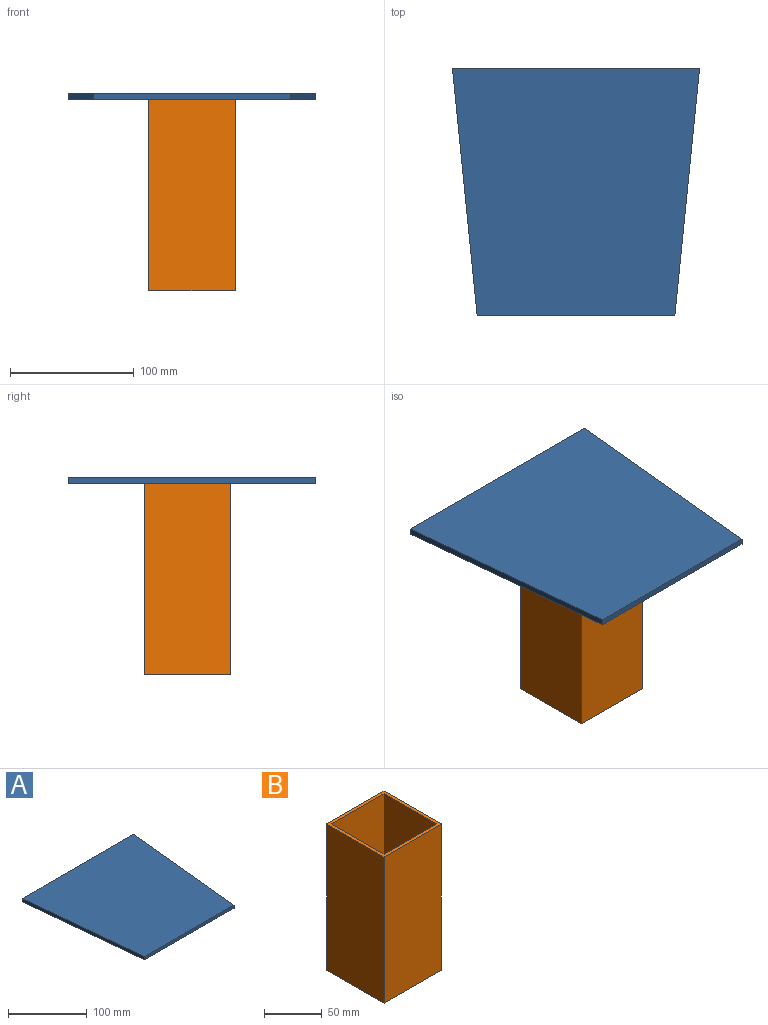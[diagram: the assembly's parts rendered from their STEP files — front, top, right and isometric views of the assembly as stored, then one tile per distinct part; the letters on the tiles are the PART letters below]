
ASSEMBLY  parts=2 mates=1
PART A: 6 faces, bbox 200x200x5 mm
  f0: plane 160x5mm, normal (0,-1,0), area 800mm2, adj f1,f3,f4,f5
  f1: plane 200x20mm, normal (1,-0.1,0), area 1005mm2, adj f0,f2,f4,f5
  f2: plane 200x5mm, normal (0,1,0), area 1000mm2, adj f1,f3,f4,f5
  f3: plane 200x20mm, normal (-1,-0.1,0), area 1005mm2, adj f0,f2,f4,f5
  f4: plane 200x200mm, normal (0,0,1), area 36000mm2, adj f0,f1,f2,f3
  f5: plane 200x200mm, normal (0,0,-1), area 36000mm2, adj f0,f1,f2,f3
PART B: 10 faces, bbox 70x70x155 mm
  f0: plane 155x64mm, normal (1,0,0), area 9920mm2, adj f1,f7,f8,f9
  f1: plane 155x64mm, normal (0,-1,0), area 9920mm2, adj f0,f2,f8,f9
  f2: plane 155x64mm, normal (-1,0,0), area 9920mm2, adj f1,f7,f8,f9
  f3: plane 155x70mm, normal (1,0,0), area 10850mm2, adj f4,f6,f8,f9
  f4: plane 155x70mm, normal (0,1,0), area 10850mm2, adj f3,f5,f8,f9
  f5: plane 155x70mm, normal (-1,0,0), area 10850mm2, adj f4,f6,f8,f9
  f6: plane 155x70mm, normal (0,-1,0), area 10850mm2, adj f3,f5,f8,f9
  f7: plane 155x64mm, normal (0,1,0), area 9920mm2, adj f0,f2,f8,f9
  f8: plane 70x70mm, normal (0,0,-1), area 804mm2, adj f0,f1,f2,f3,f4,f5,f6,f7
  f9: plane 70x70mm, normal (0,0,1), area 804mm2, adj f0,f1,f2,f3,f4,f5,f6,f7
PLACE A at identity
PLACE B t=(0,3.7,0)mm
MATE fastened B.f9 <-> A.f5  axis (0,0,1) through (265,3.7,40)mm
